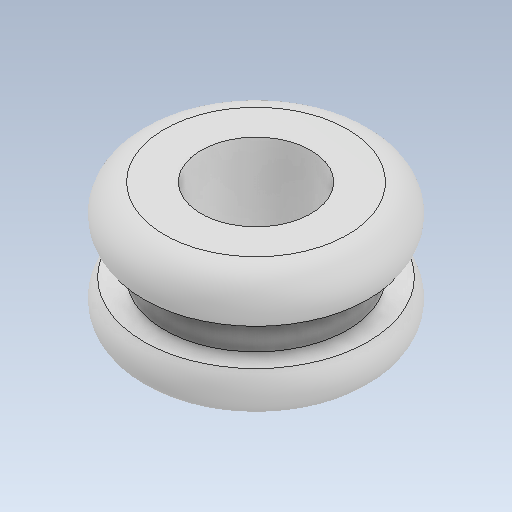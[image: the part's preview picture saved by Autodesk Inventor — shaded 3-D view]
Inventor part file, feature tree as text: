
AUTODESK INVENTOR PART (.ipt)
format: ipt  version: 2021 (Build 250183000, 183)  size: 185,856 bytes
history: mixed  units: in
note: dims shown in document units (in); Inventor stores cm internally (conversion verified against a paired STEP export)
features: revolve x1, imported_body x1
ambient origin geometry x8: Origin, YZ Plane, XZ Plane, XY Plane, X Axis, Y Axis, Z Axis, Center Point
bodies: Solid1 (imported_parasolid)
feature tree (2):
  revolve  "Revolve1"  [1 undecoded]
  imported_body  NMx_Import_Brep_tag  [imported B-rep: ~8 faces, bbox_mm=[0.0, 5.55625, 2.474939]]
note: 1 required parameter value undecoded (feature->parameter linkage not recoverable at this tier; creation-order binding heuristic only, values carry confidence <= 0.55)
